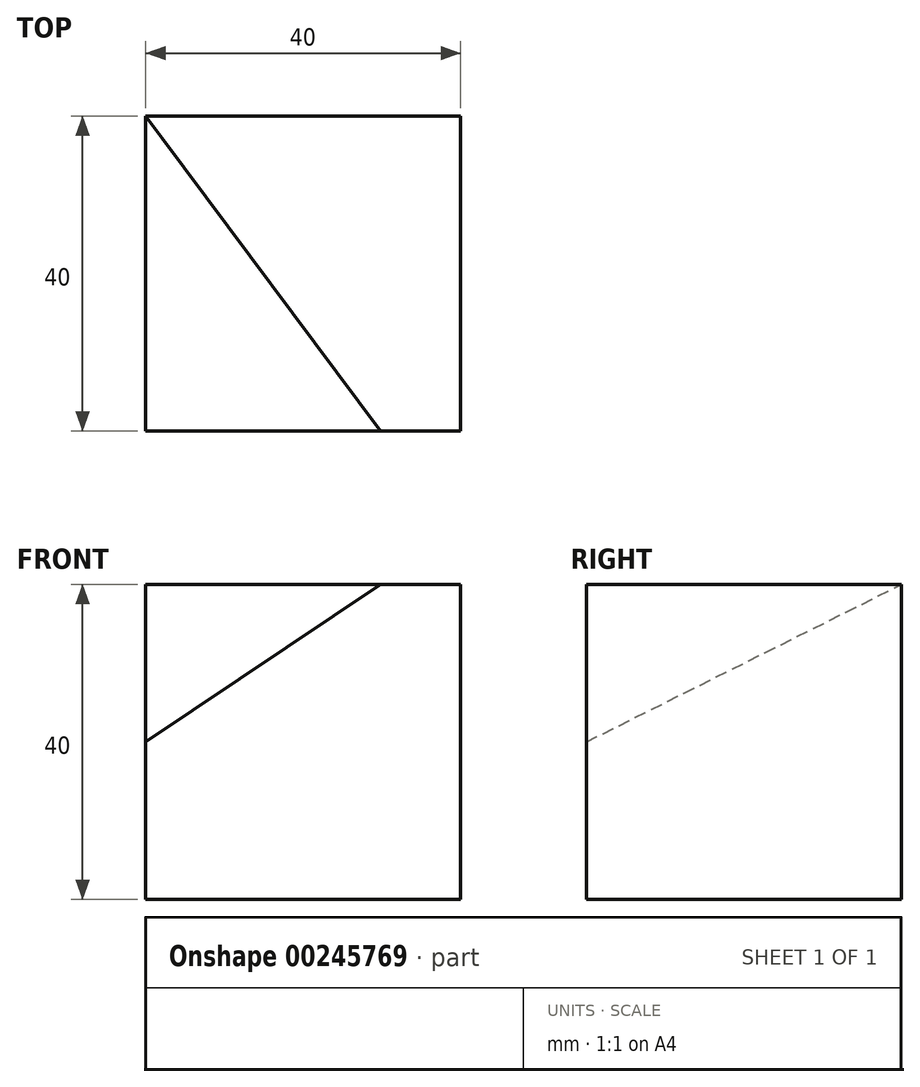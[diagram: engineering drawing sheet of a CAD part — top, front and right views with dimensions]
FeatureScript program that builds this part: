
annotation { "Feature Type Name" : "Feature", "Feature Type Description" : "" }
export const myFeature = defineFeature(function(context is Context, id is Id, definition is map)
    precondition{}
    {
        {
            var Q0;
            Q0=qCreatedBy(makeId("Top.planeOp"),FACE);
            var sketch = newSketch(context, id + "F0", { "sketchPlane" : qUnion([Q0])});
            skLineSegment(sketch, "E0", {"start": v(0, 0) * mm, "end": v(40, 0) * mm});
            skLineSegment(sketch, "E1", {"start": v(40, 0) * mm, "end": v(40, -40) * mm});
            skLineSegment(sketch, "E2", {"start": v(40, -40) * mm, "end": v(0, -40) * mm});
            skLineSegment(sketch, "E3", {"start": v(0, -40) * mm, "end": v(0, 0) * mm});
            skSolve(sketch);
        }
        {
            var Q0;
            Q0=makeQuery(id+"F0.imprint","IMPRINT",FACE,{"disambiguationData":[TD([[makeQuery(id+"F0.imprint","IMPRINT",EDGE,{"derivedFrom":sQuery(id+"F0.wireOp",EDGE,"E0")}),-1.0]])]});
            extrude(context, id + "F1", {"entities" : qUnion([Q0]), "depth" : 40 * mm});
        }
        {
            var Q0;
            Q0=makeQuery(id+"F1.opExtrude","SWEPT_FACE",FACE,{"disambiguationData":[OSD([sQuery(id+"F0.wireOp",EDGE,"E3")])]});
            var sketch = newSketch(context, id + "F2", { "sketchPlane" : qUnion([Q0])});
            skLineSegment(sketch, "E4", {"start": v(40, 20) * mm, "end": v(0, 40) * mm});
            skLineSegment(sketch, "E5", {"start": v(40, 20) * mm, "end": v(40, 40) * mm});
            skSolve(sketch);
        }
        {
            var Q0;
            Q0=makeQuery(id+"F1.opExtrude","CAP_FACE",FACE,{"disambiguationData":[OSD([sQuery(id+"F0.wireOp",EDGE,"E0"),sQuery(id+"F0.wireOp",EDGE,"E1"),sQuery(id+"F0.wireOp",EDGE,"E2"),sQuery(id+"F0.wireOp",EDGE,"E3")])],"isStart":false});
            var sketch = newSketch(context, id + "F3", { "sketchPlane" : qUnion([Q0])});
            skLineSegment(sketch, "E6", {"start": v(29.82, -40) * mm, "end": v(0, 0) * mm});
            skLineSegment(sketch, "E7", {"start": v(29.82, -40) * mm, "end": v(0, -40) * mm});
            skLineSegment(sketch, "E8", {"start": v(0, -40) * mm, "end": v(0, 0) * mm});
            skSolve(sketch);
        }
        {
            var Q0;
            Q0=sQuery(id+"F3.wireOp",VERTEX,"E7.start");
            var Q1;
            Q1=sQuery(id+"F2.wireOp",VERTEX,"E5.start");
            var Q2;
            Q2=sQuery(id+"F3.wireOp",VERTEX,"E8.end");
            cPlane(context, id + "F4", {"entities" : qUnion([Q0, Q1, Q2]), "cplaneType" : CPlaneType.THREE_POINT, "offset" : 25 * mm, "width" : 150 * mm, "height" : 150 * mm});
        }
        {
            var Q0;
            Q0=qCreatedBy(id+"F4.planeOp",FACE);
            var sketch = newSketch(context, id + "F5", { "sketchPlane" : qUnion([Q0])});
            skLineSegment(sketch, "E9", {"start": v(53.3, -17.95) * mm, "end": v(18.4, 17.89) * mm});
            skLineSegment(sketch, "E10", {"start": v(18.4, 17.89) * mm, "end": v(18.34, -26.93) * mm});
            skLineSegment(sketch, "E11", {"start": v(18.34, -26.93) * mm, "end": v(53.3, -17.95) * mm});
            skSolve(sketch);
        }
        {
            var Q0;
            Q0 = qSketchRegion(id + "F5", true);
            extrude(context, id + "F6", {"entities" : qUnion([Q0]), "operationType" : NewBodyOperationType.REMOVE, "depth" : 25 * mm});
        }
    });
